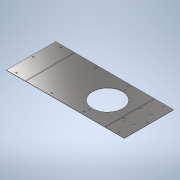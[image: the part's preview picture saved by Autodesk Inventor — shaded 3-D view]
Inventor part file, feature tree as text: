
AUTODESK INVENTOR PART (.ipt)
format: ipt  version: 2020 (Build 240168000, 168)  size: 208,384 bytes
history: native  units: mm
features: sheet_metal_op x8, sketch x7, hole x3, other x3, extrude x1
ambient origin geometry x8: Origin, YZ Plane, XZ Plane, XY Plane, X Axis, Y Axis, Z Axis, Center Point
bodies: Solid1 (feature_tree)
feature tree (22):
  sheet_metal_op  "Face1"
  sheet_metal_op  "Flange1"
  sheet_metal_op  "Flange2"
  extrude  "Extrusion1"  Depth=155.0mm
  hole  "Hole1"  [1 undecoded]
  hole  "Hole2"  [1 undecoded]
  hole  "Hole3"  [1 undecoded]
  sheet_metal_op  "Unfold2"
  sketch  "Sketch1"  dims[d0=252.0mm d1=155.0mm]
  other  "Plate1"
  sketch  "Sketch2"  dims[d2=1.0mm d3=1.0mm]
  other  "Plate2"
  sheet_metal_op  "Bend1"
  sheet_metal_op  "Corner1"
  sketch  "Sketch3"  dims[d4=0.5mm d5=2.0mm]
  other  "Plate3"
  sheet_metal_op  "Bend2"
  sheet_metal_op  "Corner2"
  sketch  "Sketch4"  dims[d6=1.0mm d7=61.0mm d8=90.0deg d9=1.0mm]
  sketch  "Sketch5"  dims[d10=4.0mm]
  sketch  "Sketch6"  dims[d11=1.0mm]
  sketch  "Sketch7"  dims[d12=1.0mm d13=1.0mm d14=0.5mm d15=2.0mm d16=1.0mm d17=61.0mm d18=90.0deg d19=1.0mm d20=4.0mm d21=1.0mm d22=1.0mm d23=77.5mm d24=71.0mm d25=94.0mm d26=55.5mm d27=55.5mm d28=4.5mm d29=4.5mm d30=0.0mm d31=0.0mm d32=75.0mm d33=75.0mm d34=8.0mm d35=8.0mm d36=4.5mm d37=12.0mm d38=4.0mm d39=2.0mm d40=90.0deg d41=1.0mm d42=20.594885mm d43=77.5mm d44=7.0mm d45=8.0mm d46=8.0mm d47=24.0mm d48=24.0mm d49=4.5mm d50=12.0mm d51=4.0mm d52=2.0mm d53=90.0deg d54=1.0mm d55=20.594885mm d57=35.0mm d58=45.0mm d59=70.0mm d60=7.0mm d61=7.0mm d62=7.0mm d63=7.0mm d64=6.0mm d65=12.0mm d66=4.0mm d67=2.0mm d68=90.0deg d69=1.0mm d70=20.594885mm]
note: 3 required parameter values undecoded (feature->parameter linkage not recoverable at this tier; creation-order binding heuristic only, values carry confidence <= 0.55)
